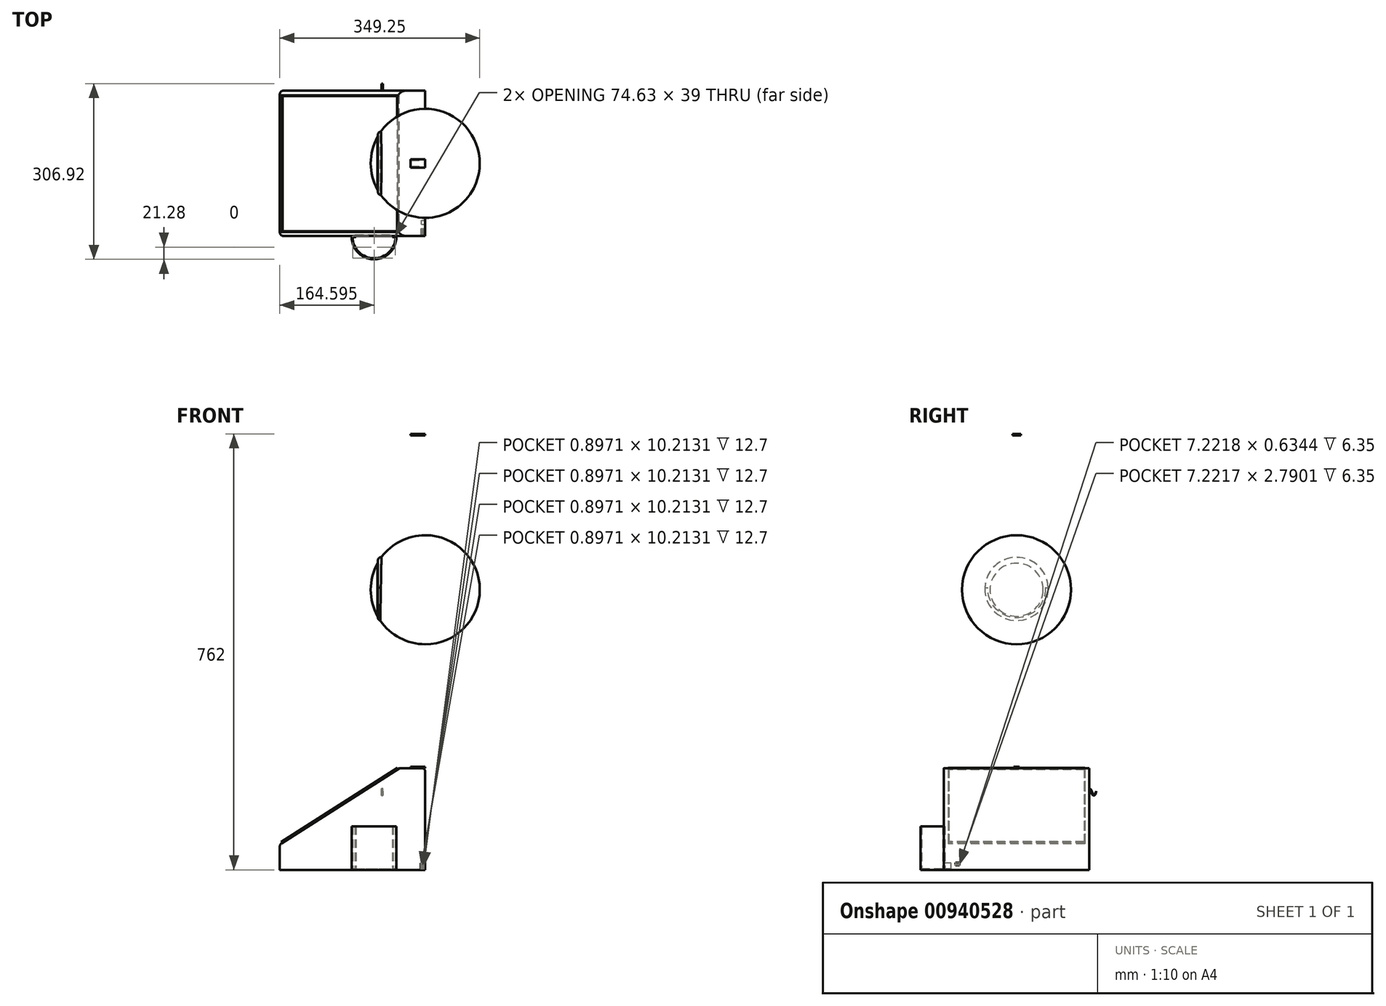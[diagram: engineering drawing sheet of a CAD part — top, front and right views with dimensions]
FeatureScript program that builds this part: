
annotation { "Feature Type Name" : "Feature", "Feature Type Description" : "" }
export const myFeature = defineFeature(function(context is Context, id is Id, definition is map)
    precondition{}
    {
        {
            var Q0;
            Q0=qCreatedBy(makeId("Front.planeOp"),FACE);
            var sketch = newSketch(context, id + "F0", { "sketchPlane" : qUnion([Q0])});
            skLineSegment(sketch, "E0", {"start": v(0, 0) * mm, "end": v(-254, 0) * mm});
            skLineSegment(sketch, "E1", {"start": v(0, 0) * mm, "end": v(0, 177.8) * mm});
            skLineSegment(sketch, "E2", {"start": v(-254, 0) * mm, "end": v(-254, 44.45) * mm});
            skLineSegment(sketch, "E3", {"start": v(0, 177.8) * mm, "end": v(-44.45, 177.8) * mm});
            skLineSegment(sketch, "E4", {"start": v(-254, 44.45) * mm, "end": v(-44.45, 177.8) * mm});
            skSolve(sketch);
        }
        {
            var Q0;
            Q0=makeQuery(id+"F0.imprint","IMPRINT",FACE,{"disambiguationData":[TD([[makeQuery(id+"F0.imprint","IMPRINT",EDGE,{"derivedFrom":sQuery(id+"F0.wireOp",EDGE,"E0")}),-1.0]])]});
            extrude(context, id + "F1", {"entities" : qUnion([Q0]), "depth" : 127 * mm, "offsetDistance" : 25.4 * mm, "hasSecondDirection" : true, "secondDirectionOppositeDirection" : true, "secondDirectionDepth" : 127 * mm});
        }
        {
            var Q0;
            Q0=makeQuery(id+"F1.opExtrude","SWEPT_EDGE",EDGE,{"disambiguationData":[OSD([sQuery(id+"F0.wireOp",EDGE,"E3"),sQuery(id+"F0.wireOp",EDGE,"E4")])]});
            var Q1;
            Q1=makeQuery(id+"F1.opExtrude","SWEPT_EDGE",EDGE,{"disambiguationData":[OSD([sQuery(id+"F0.wireOp",EDGE,"E1"),sQuery(id+"F0.wireOp",EDGE,"E3")])]});
            var Q2;
            Q2=makeQuery(id+"F1.opExtrude","SWEPT_EDGE",EDGE,{"disambiguationData":[OSD([sQuery(id+"F0.wireOp",EDGE,"E2"),sQuery(id+"F0.wireOp",EDGE,"E4")])]});
            var Q3;
            Q3=makeQuery(id+"F1.opExtrude","CAP_EDGE",EDGE,{"disambiguationData":[OSD([sQuery(id+"F0.wireOp",EDGE,"E2")])],"isStart":true});
            var Q4;
            Q4=makeQuery(id+"F1.opExtrude","CAP_EDGE",EDGE,{"disambiguationData":[OSD([sQuery(id+"F0.wireOp",EDGE,"E4")])],"isStart":true});
            var Q5;
            Q5=makeQuery(id+"F1.opExtrude","CAP_EDGE",EDGE,{"disambiguationData":[OSD([sQuery(id+"F0.wireOp",EDGE,"E4")])],"isStart":false});
            var Q6;
            Q6=makeQuery(id+"F1.opExtrude","CAP_EDGE",EDGE,{"disambiguationData":[OSD([sQuery(id+"F0.wireOp",EDGE,"E2")])],"isStart":false});
            fillet(context, id + "F2", {"entities" : qUnion([Q0, Q1, Q2, Q3, Q4, Q5, Q6]), "radius" : 6.35 * mm, "tangentPropagation" : true, "allowEdgeOverflow" : false});
        }
        {
            var Q0;
            Q0=makeQuery(id+"F1.opExtrude","SWEPT_FACE",FACE,{"disambiguationData":[OSD([sQuery(id+"F0.wireOp",EDGE,"E4")])]});
            var sketch = newSketch(context, id + "F3", { "sketchPlane" : qUnion([Q0])});
            skLineSegment(sketch, "E5.bottom", {"start": v(53.87, 117.8) * mm, "end": v(-184.89, 117.8) * mm});
            skLineSegment(sketch, "E5.top", {"start": v(53.87, -118.41) * mm, "end": v(-184.89, -118.41) * mm});
            skLineSegment(sketch, "E5.left", {"start": v(53.87, 117.8) * mm, "end": v(53.87, -118.41) * mm});
            skLineSegment(sketch, "E5.right", {"start": v(-184.89, 117.8) * mm, "end": v(-184.89, -118.41) * mm});
            skSolve(sketch);
        }
        {
            var Q0;
            Q0=makeQuery(id+"F3.imprint","IMPRINT",FACE,{"disambiguationData":[TD([[makeQuery(id+"F3.imprint","IMPRINT",EDGE,{"derivedFrom":sQuery(id+"F3.wireOp",EDGE,"E5.bottom")}),1.0]])]});
            extrude(context, id + "F4", {"entities" : qUnion([Q0]), "depth" : 2.54 * mm, "offsetDistance" : 25.4 * mm});
        }
        {
            var Q0;
            Q0=makeQuery(id+"F4.opExtrude","CAP_FACE",FACE,{"disambiguationData":[OSD([sQuery(id+"F3.wireOp",EDGE,"E5.bottom"),sQuery(id+"F3.wireOp",EDGE,"E5.top"),sQuery(id+"F3.wireOp",EDGE,"E5.left"),sQuery(id+"F3.wireOp",EDGE,"E5.right")])],"isStart":false});
            var Q1;
            Q1=makeQuery(id+"F4.opExtrude","SWEPT_BODY",BODY,{"disambiguationData":[OSD([sQuery(id+"F3.wireOp",EDGE,"E5.bottom"),sQuery(id+"F3.wireOp",EDGE,"E5.top"),sQuery(id+"F3.wireOp",EDGE,"E5.left"),sQuery(id+"F3.wireOp",EDGE,"E5.right")])]});
            shell(context, id + "F5", {"entities" : qUnion([Q0]), "parts" : qUnion([Q1]), "thickness" : 1.27 * mm, "oppositeDirection" : true});
        }
        {
            var Q0;
            Q0=qCreatedBy(makeId("Right.planeOp"),FACE);
            var sketch = newSketch(context, id + "F6", { "sketchPlane" : qUnion([Q0])});
            skLineSegment(sketch, "E6", {"start": v(0, 0) * mm, "end": v(0, 762) * mm, "construction": true});
            skLineSegment(sketch, "E7", {"start": v(0, 177.8) * mm, "end": v(0, 762) * mm, "construction": true});
            skLineSegment(sketch, "E8", {"start": v(0, 762) * mm, "end": v(-177.06, 762) * mm});
            skLineSegment(sketch, "E9", {"start": v(0, 762) * mm, "end": v(82.25, 762) * mm});
            skLineSegment(sketch, "E10.bottom", {"start": v(0, 762) * mm, "end": v(-7.34, 762) * mm});
            skLineSegment(sketch, "E10.top", {"start": v(0, 759.04) * mm, "end": v(-7.34, 759.04) * mm});
            skLineSegment(sketch, "E10.left", {"start": v(0, 762) * mm, "end": v(0, 759.04) * mm});
            skLineSegment(sketch, "E10.right", {"start": v(-7.34, 762) * mm, "end": v(-7.34, 759.04) * mm});
            skLineSegment(sketch, "E11.MirrorCS", {"start": v(0, 759.04) * mm, "end": v(7.34, 759.04) * mm});
            skLineSegment(sketch, "E12.MirrorCS", {"start": v(7.34, 762) * mm, "end": v(7.34, 759.04) * mm});
            skLineSegment(sketch, "E13.bottom", {"start": v(0, 177.8) * mm, "end": v(-5.09, 177.8) * mm});
            skLineSegment(sketch, "E13.top", {"start": v(0, 180.17) * mm, "end": v(-5.09, 180.17) * mm});
            skLineSegment(sketch, "E13.left", {"start": v(0, 177.8) * mm, "end": v(0, 180.17) * mm});
            skLineSegment(sketch, "E13.right", {"start": v(-5.09, 177.8) * mm, "end": v(-5.09, 180.17) * mm});
            skLineSegment(sketch, "E14.MirrorCS", {"start": v(0, 180.17) * mm, "end": v(5.09, 180.17) * mm});
            skLineSegment(sketch, "E15.MirrorCS", {"start": v(5.09, 177.8) * mm, "end": v(5.09, 180.17) * mm});
            skLineSegment(sketch, "E16.MirrorCS", {"start": v(0, 177.8) * mm, "end": v(5.09, 177.8) * mm});
            skSolve(sketch);
        }
        {
            var Q0;
            Q0 = qSketchRegion(id + "F6", true);
            extrude(context, id + "F7", {"entities" : qUnion([Q0]), "oppositeDirection" : true, "depth" : 25.4 * mm, "offsetDistance" : 25.4 * mm});
        }
        {
            var Q0;
            Q0=sQuery(id+"F6.wireOp",EDGE,"E7");
            cPlane(context, id + "F8", {"entities" : qUnion([Q0]), "cplaneType" : CPlaneType.LINE_ANGLE, "offset" : 25.4 * mm, "angle" : 0 * degree, "width" : 152.4 * mm, "height" : 152.4 * mm});
        }
        {
            var Q0;
            Q0=qCreatedBy(id+"F8.planeOp",FACE);
            var sketch = newSketch(context, id + "F9", { "sketchPlane" : qUnion([Q0])});
            skCircle(sketch, "E17", {"center": v(0, 489.5) * mm, "radius": 95.25 * mm});
            skLineSegment(sketch, "E18", {"start": v(0, 489.5) * mm, "end": v(0, 394.25) * mm});
            skLineSegment(sketch, "E19", {"start": v(0, 394.25) * mm, "end": v(0, 584.75) * mm});
            skSolve(sketch);
        }
        {
            var Q0;
            {var subQ0=sQuery(id+"F9.wireOp",EDGE,"E19");var subQ4=makeQuery(id+"F9.imprint","IMPRINT",VERTEX,{"derivedFrom":subQ0});Q0=makeQuery(id+"F9.imprint","IMPRINT",FACE,{"disambiguationData":[TD([[makeQuery(id+"F9.imprint","IMPRINT",EDGE,{"disambiguationData":[TD([[subQ4,1.0]])],"derivedFrom":subQ0}),1.0]])]});}
            var Q1;
            Q1=sQuery(id+"F6.wireOp",EDGE,"E7");
            revolve(context, id + "F10", {"surfaceOperationType" : NewSurfaceOperationType.NEW, "entities" : qUnion([Q0]), "axis" : qUnion([Q1]), "revolveType" : RevolveType.FULL});
        }
        {
            var Q0;
            Q0=qCreatedBy(id+"F8.planeOp",FACE);
            cPlane(context, id + "F11", {"entities" : qUnion([Q0]), "cplaneType" : CPlaneType.OFFSET, "offset" : 76.2 * mm, "oppositeDirection" : true, "width" : 152.4 * mm, "height" : 152.4 * mm});
        }
        {
            var Q0;
            Q0=qCreatedBy(id+"F11.planeOp",FACE);
            var sketch = newSketch(context, id + "F12", { "sketchPlane" : qUnion([Q0])});
            skCircle(sketch, "E20", {"center": v(0, 490.95) * mm, "radius": 55.34 * mm});
            skSolve(sketch);
        }
        {
            var Q0;
            Q0 = qSketchRegion(id + "F12", true);
            extrude(context, id + "F13", {"entities" : qUnion([Q0]), "operationType" : NewBodyOperationType.ADD, "oppositeDirection" : true, "depth" : 6.35 * mm, "offsetDistance" : 25.4 * mm});
        }
        {
            var Q0;
            Q0=makeQuery(id+"F13.opExtrude","CAP_EDGE",EDGE,{"disambiguationData":[OSD([sQuery(id+"F12.wireOp",EDGE,"E20")])],"isStart":false});
            var Q1;
            Q1=makeQuery(id+"F13.boolean.opBoolean","INTERSECT",EDGE,{"derivedFrom":[makeQuery(id+"F10.opRevolve","SWEPT_FACE",FACE,{"disambiguationData":[OSD([sQuery(id+"F9.wireOp",EDGE,"E17")])]}),makeQuery(id+"F13.opExtrude","CAP_FACE",FACE,{"disambiguationData":[OSD([sQuery(id+"F12.wireOp",EDGE,"E20")])],"isStart":false})]});
            fillet(context, id + "F14", {"entities" : qUnion([Q0, Q1]), "radius" : 5.08 * mm, "tangentPropagation" : true, "allowEdgeOverflow" : false});
        }
        {
            var Q0;
            Q0=makeQuery(id+"F1.opExtrude","CAP_FACE",FACE,{"disambiguationData":[OSD([sQuery(id+"F0.wireOp",EDGE,"E0"),sQuery(id+"F0.wireOp",EDGE,"E1"),sQuery(id+"F0.wireOp",EDGE,"E2"),sQuery(id+"F0.wireOp",EDGE,"E3"),sQuery(id+"F0.wireOp",EDGE,"E4")])],"isStart":false});
            var sketch = newSketch(context, id + "F15", { "sketchPlane" : qUnion([Q0])});
            skLineSegment(sketch, "E21.bottom", {"start": v(-1.79, 1.51) * mm, "end": v(-2.68, 1.51) * mm});
            skLineSegment(sketch, "E21.top", {"start": v(-1.79, 11.73) * mm, "end": v(-2.68, 11.73) * mm});
            skLineSegment(sketch, "E21.left", {"start": v(-1.79, 1.51) * mm, "end": v(-1.79, 11.73) * mm});
            skLineSegment(sketch, "E21.right", {"start": v(-2.68, 1.51) * mm, "end": v(-2.68, 11.73) * mm});
            skLineSegment(sketch, "E22", {"start": v(-3.07, 11.7) * mm, "end": v(-3.07, 4.96) * mm, "construction": true});
            skLineSegment(sketch, "E23.MirrorCS", {"start": v(-3.46, 1.51) * mm, "end": v(-3.46, 11.73) * mm});
            skLineSegment(sketch, "E24.MirrorCS", {"start": v(-4.35, 11.73) * mm, "end": v(-3.46, 11.73) * mm});
            skLineSegment(sketch, "E25.MirrorCS", {"start": v(-4.35, 1.51) * mm, "end": v(-4.35, 11.73) * mm});
            skLineSegment(sketch, "E26.MirrorCS", {"start": v(-4.35, 1.51) * mm, "end": v(-3.46, 1.51) * mm});
            skLineSegment(sketch, "E27", {"start": v(-4.7, 11.75) * mm, "end": v(-4.7, 9.75) * mm, "construction": true});
            skLineSegment(sketch, "E28.MirrorCS", {"start": v(-5.04, 1.51) * mm, "end": v(-5.04, 11.73) * mm});
            skLineSegment(sketch, "E29.MirrorCS", {"start": v(-6.7, 1.51) * mm, "end": v(-6.7, 11.73) * mm});
            skLineSegment(sketch, "E30.MirrorCS", {"start": v(-5.93, 1.51) * mm, "end": v(-5.93, 11.73) * mm});
            skLineSegment(sketch, "E31.MirrorCS", {"start": v(-7.6, 1.51) * mm, "end": v(-7.6, 11.73) * mm});
            skLineSegment(sketch, "E32.MirrorCS", {"start": v(-7.6, 11.73) * mm, "end": v(-6.7, 11.73) * mm});
            skLineSegment(sketch, "E33.MirrorCS", {"start": v(-5.04, 11.73) * mm, "end": v(-5.93, 11.73) * mm});
            skLineSegment(sketch, "E34.MirrorCS", {"start": v(-5.04, 1.51) * mm, "end": v(-5.93, 1.51) * mm});
            skLineSegment(sketch, "E35.MirrorCS", {"start": v(-7.6, 1.51) * mm, "end": v(-6.7, 1.51) * mm});
            skSolve(sketch);
        }
        {
            var Q0;
            Q0=makeQuery(id+"F15.imprint","IMPRINT",FACE,{"disambiguationData":[TD([[makeQuery(id+"F15.imprint","IMPRINT",EDGE,{"derivedFrom":sQuery(id+"F15.wireOp",EDGE,"E29.MirrorCS")}),1.0]])]});
            var Q1;
            Q1=makeQuery(id+"F15.imprint","IMPRINT",FACE,{"disambiguationData":[TD([[makeQuery(id+"F15.imprint","IMPRINT",EDGE,{"derivedFrom":sQuery(id+"F15.wireOp",EDGE,"E28.MirrorCS")}),1.0]])]});
            var Q2;
            Q2=makeQuery(id+"F15.imprint","IMPRINT",FACE,{"disambiguationData":[TD([[makeQuery(id+"F15.imprint","IMPRINT",EDGE,{"derivedFrom":sQuery(id+"F15.wireOp",EDGE,"E23.MirrorCS")}),1.0]])]});
            var Q3;
            Q3=makeQuery(id+"F15.imprint","IMPRINT",FACE,{"disambiguationData":[TD([[makeQuery(id+"F15.imprint","IMPRINT",EDGE,{"derivedFrom":sQuery(id+"F15.wireOp",EDGE,"E21.bottom")}),-1.0]])]});
            extrude(context, id + "F16", {"entities" : qUnion([Q0, Q1, Q2, Q3]), "operationType" : NewBodyOperationType.REMOVE, "oppositeDirection" : true, "depth" : 12.7 * mm, "offsetDistance" : 25.4 * mm});
        }
        {
            var Q0;
            Q0=qCreatedBy(makeId("Top.planeOp"),FACE);
            var sketch = newSketch(context, id + "F17", { "sketchPlane" : qUnion([Q0])});
            skLineSegment(sketch, "E36", {"start": v(-50.34, -127.16) * mm, "end": v(-128.47, -127.16) * mm});
            skArc(sketch, "E37", {"start": v(-128.47, -127.16) * mm, "mid": v(-89.4, -167.76) * mm, "end": v(-50.34, -127.16) * mm});
            skLineSegment(sketch, "E38", {"start": v(-122.67, -127.16) * mm, "end": v(-122.67, -125.2) * mm});
            skLineSegment(sketch, "E39", {"start": v(-122.67, -125.2) * mm, "end": v(-55.88, -125.2) * mm});
            skLineSegment(sketch, "E40", {"start": v(-55.88, -125.2) * mm, "end": v(-55.88, -127.16) * mm});
            skSolve(sketch);
        }
        {
            var Q0;
            Q0 = qSketchRegion(id + "F17", true);
            extrude(context, id + "F18", {"entities" : qUnion([Q0]), "depth" : 76.2 * mm, "offsetDistance" : 25.4 * mm});
        }
        {
            var Q0;
            Q0=makeQuery(id+"F18.opExtrude","CAP_FACE",FACE,{"disambiguationData":[OSD([sQuery(id+"F17.wireOp",EDGE,"E36"),sQuery(id+"F17.wireOp",EDGE,"E37"),sQuery(id+"F17.wireOp",EDGE,"E38"),sQuery(id+"F17.wireOp",EDGE,"E39"),sQuery(id+"F17.wireOp",EDGE,"E40")])],"isStart":false});
            shell(context, id + "F19", {"entities" : qUnion([Q0]), "thickness" : 1.78 * mm});
        }
        {
            var Q0;
            Q0=makeQuery(id+"F1.opExtrude","SWEPT_FACE",FACE,{"disambiguationData":[OSD([sQuery(id+"F0.wireOp",EDGE,"E1")])]});
            var sketch = newSketch(context, id + "F20", { "sketchPlane" : qUnion([Q0])});
            skLineSegment(sketch, "E41.bottom", {"start": v(-106.88, 12.48) * mm, "end": v(-99.66, 12.48) * mm});
            skLineSegment(sketch, "E41.top", {"start": v(-106.88, 9.69) * mm, "end": v(-99.66, 9.69) * mm});
            skLineSegment(sketch, "E41.left", {"start": v(-106.88, 12.48) * mm, "end": v(-106.88, 9.69) * mm});
            skLineSegment(sketch, "E41.right", {"start": v(-99.66, 12.48) * mm, "end": v(-99.66, 9.69) * mm});
            skLineSegment(sketch, "E42.bottom", {"start": v(-106.87, 8.91) * mm, "end": v(-99.65, 8.91) * mm});
            skLineSegment(sketch, "E42.top", {"start": v(-106.87, 8.28) * mm, "end": v(-99.65, 8.28) * mm});
            skLineSegment(sketch, "E42.left", {"start": v(-106.87, 8.91) * mm, "end": v(-106.87, 8.28) * mm});
            skLineSegment(sketch, "E42.right", {"start": v(-99.65, 8.91) * mm, "end": v(-99.65, 8.28) * mm});
            skSolve(sketch);
        }
        {
            var Q0;
            Q0 = qSketchRegion(id + "F20", true);
            extrude(context, id + "F21", {"entities" : qUnion([Q0]), "operationType" : NewBodyOperationType.REMOVE, "oppositeDirection" : true, "depth" : 6.35 * mm, "offsetDistance" : 25.4 * mm});
        }
        {
            var Q0;
            Q0=qCreatedBy(id+"F11.planeOp",FACE);
            var sketch = newSketch(context, id + "F22", { "sketchPlane" : qUnion([Q0])});
            skLineSegment(sketch, "E43", {"start": v(126.16, 142.26) * mm, "end": v(126.16, 135.43) * mm});
            skFitSpline(sketch, "E44", {"points": [v(126.16, 135.43) * mm, v(127.91, 136.9) * mm, v(129.43, 137.6) * mm, v(131.43, 135.43) * mm, v(132.05, 131.52) * mm, v(136.2, 130.42) * mm, v(139.16, 137.6) * mm], "startDerivative": vector(13.38, 11.32) * mm, "endDerivative": vector(7.03, 38.63) * mm});
            skFitSpline(sketch, "E45", {"points": [v(139.16, 137.6) * mm, v(138.33, 136.28) * mm, v(137.64, 134.08) * mm, v(136.68, 131.73) * mm, v(133.99, 131.66) * mm, v(132.95, 133.73) * mm, v(130.88, 138.97) * mm, v(126.16, 142.26) * mm], "startDerivative": vector(-8.66, -12) * mm, "endDerivative": vector(-27.35, 13.4) * mm});
            skSolve(sketch);
        }
        {
            var Q0;
            Q0 = qSketchRegion(id + "F22", true);
            extrude(context, id + "F23", {"entities" : qUnion([Q0]), "operationType" : NewBodyOperationType.ADD, "depth" : 2.54 * mm, "offsetDistance" : 25.4 * mm});
        }
    });
